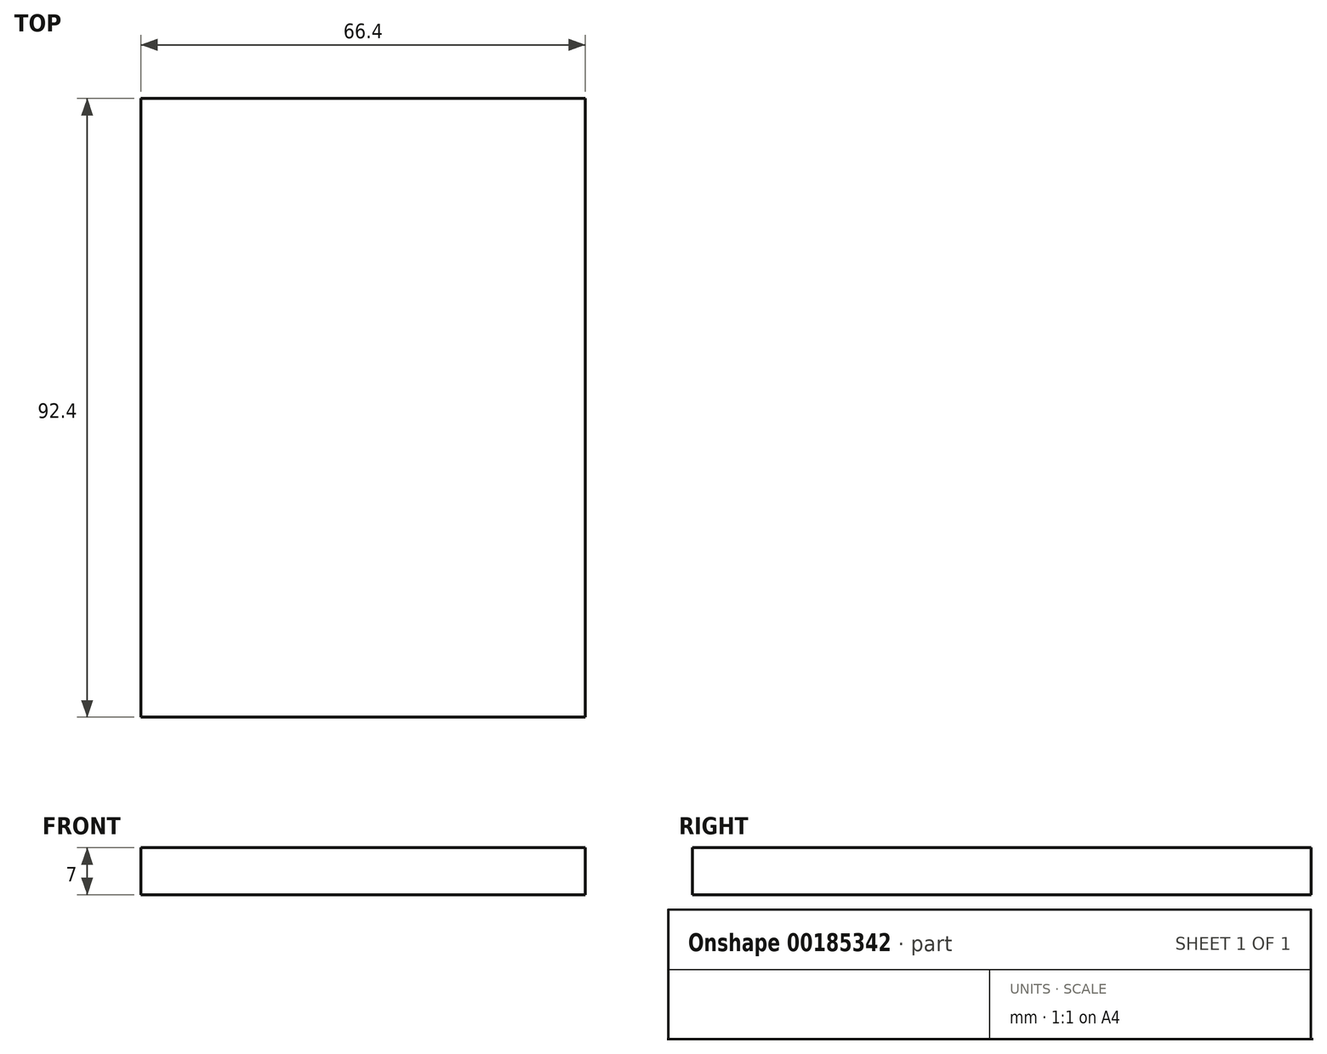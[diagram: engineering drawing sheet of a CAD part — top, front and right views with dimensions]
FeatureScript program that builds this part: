
annotation { "Feature Type Name" : "Feature", "Feature Type Description" : "" }
export const myFeature = defineFeature(function(context is Context, id is Id, definition is map)
    precondition{}
    {
        {
            var Q0;
            Q0=qCreatedBy(makeId("Top.planeOp"),FACE);
            var sketch = newSketch(context, id + "F0", { "sketchPlane" : qUnion([Q0])});
            skLineSegment(sketch, "E0.bottom", {"start": v(33.2, -46.2) * mm, "end": v(-33.2, -46.2) * mm});
            skLineSegment(sketch, "E0.top", {"start": v(33.2, 46.2) * mm, "end": v(-33.2, 46.2) * mm});
            skLineSegment(sketch, "E0.left", {"start": v(33.2, -46.2) * mm, "end": v(33.2, 46.2) * mm});
            skLineSegment(sketch, "E0.right", {"start": v(-33.2, -46.2) * mm, "end": v(-33.2, 46.2) * mm});
            skPoint(sketch, "E0.middle", {"position": v(0, 0) * mm});
            skSolve(sketch);
        }
        {
            var Q0;
            Q0=makeQuery(id+"F0.imprint","IMPRINT",FACE,{"disambiguationData":[TD([[makeQuery(id+"F0.imprint","IMPRINT",EDGE,{"derivedFrom":sQuery(id+"F0.wireOp",EDGE,"E0.bottom")}),-1.0]])]});
            extrude(context, id + "F1", {"entities" : qUnion([Q0]), "depth" : 7 * mm});
        }
    });
